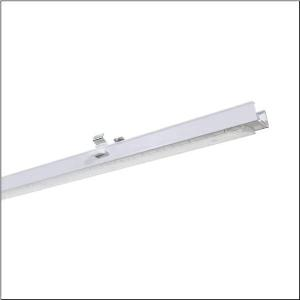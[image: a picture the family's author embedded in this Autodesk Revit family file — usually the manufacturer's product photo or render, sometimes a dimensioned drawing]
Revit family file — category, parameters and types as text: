
# Revit family: trunking_flex_31_51re12db49b
name_source: partatom
category: Lighting Fixtures
units: mm (PartAtom-declared; Revit-internal decimal feet)

## family parameters
Cut with Voids When Loaded = No
Host = Face
Light Source = No
Part Type = Normal
Room Calculation Point = No
Round Connector Dimension = Use Diameter
Shared = No

## types (1)
- --- (1 x LED, 8900 lm, 56 W, 4000K)
    Apparent Load = 56 VA
    CIE Flux Codes = 65 91 98 99 100
    Color Rendering = 80
    Color Temperature = 4000K
    Default Elevation = 1800 mm
    Description = Trunking Flex 31, luminaire insert, of extruded aluminium section, coated, traffic white (RAL 9016), length: 1.472mm, width: 91mm, height: 53mm, LED rated luminous flux: 8.900lm, light colour: 840, control gear: DALI 2, with system connector: socket, mains connection: 220..240V, AC, 50/60Hz, rated input power: 56W, primary light control with lens, of plastic, primary optical cover: cover, of PMMA, light emission: direct distribution, protection rating (complete): IP20, insulation class (complete): insulation class I (protective earthing), certification: CE, UKCA, impact resistance: IK02, permissible ambient temperature for indoor applications: -20..+40°C, packaging unit: 1 piece
    Height = 58 mm
    Lamp = 1 x LED
    Lamp Light Flux = 8900 lm
    Lamp Power = 56 W
    Lamp count = 1
    Length = 1472 mm
    Luminous efficacy = 159 lm/W
    Manufacturer = Siteco
    ModVariant = No
    Model = 51RE12DB49B
    Mounting Place = Ceiling
    Mounting Type = Pendant
    Number of Poles = 1
    OnlyDefault = Yes
    Power Factor = 1
    Product Name = Trunking Flex 31
    Product group = luminaire insert
    ProductGroupID = 901
    Protection Class = Protection class I
    Protection Degree = IP 20
    RLX_Detail_Level = 1
    RLX_Emergency_Light_Flux = 0 lm
    RLX_Emergency_Type = 0
    RLX_Emergency_Type_DB = No
    RlxData = <blob elided: 21837 chars, md5=465c9940>
    Socket = socket
    Standby Power = 0 W
    System Light Flux = 8900 lm
    System Power = 56 W
    Type Comments = individual setting: luminous flux: 100 % | (OFF | ON | OFF | OFF) | 1200 mA
    Type Image = l_1266702.jpg
    URL = http://relux.com
    VarID = @adj_018699
    Voltage = 0 V
    Weight = 0.00 kg
    Width = 65 mm

## geometry (parser evidence)
native form markers: Blend x4, Sweep x9
no freeform markers — native parametric forms only
